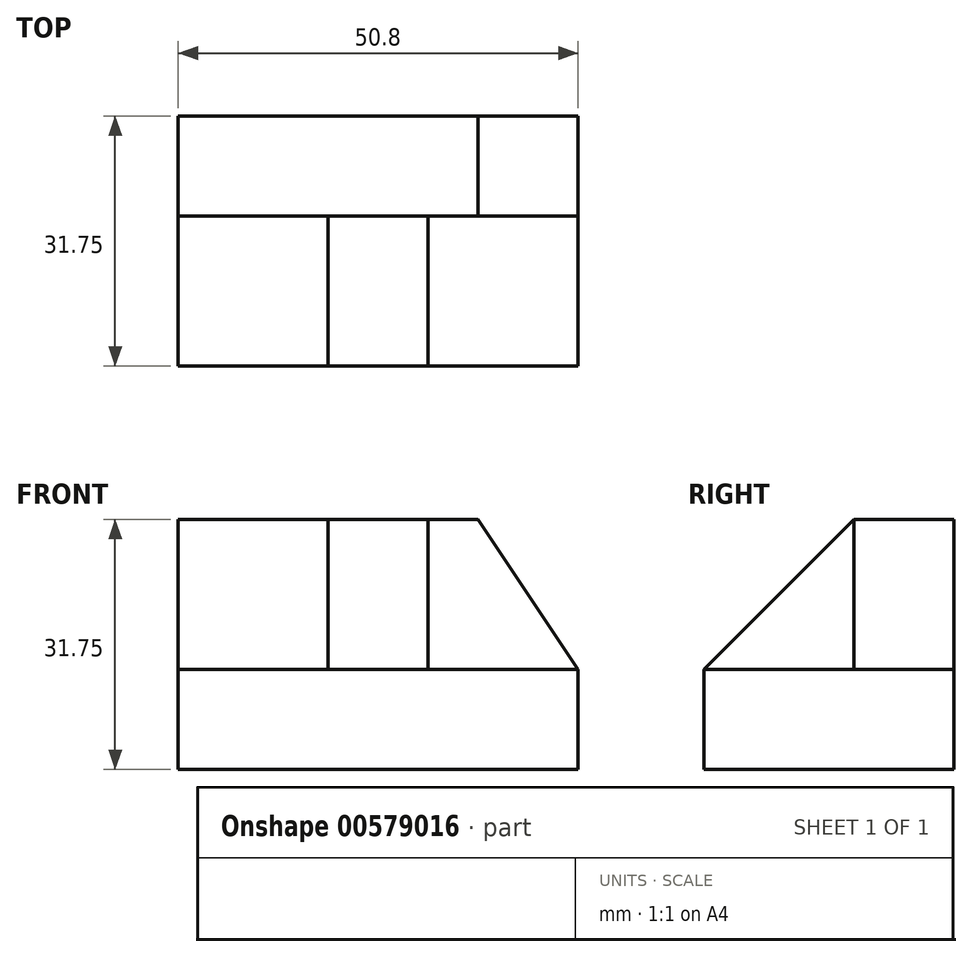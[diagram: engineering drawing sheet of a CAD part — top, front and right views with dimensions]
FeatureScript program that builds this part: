
annotation { "Feature Type Name" : "Feature", "Feature Type Description" : "" }
export const myFeature = defineFeature(function(context is Context, id is Id, definition is map)
    precondition{}
    {
        {
            var Q0;
            Q0=qCreatedBy(makeId("Front.planeOp"),FACE);
            var sketch = newSketch(context, id + "F0", { "sketchPlane" : qUnion([Q0])});
            skLineSegment(sketch, "E0", {"start": v(-68.76, 0) * mm, "end": v(-17.96, 0) * mm});
            skLineSegment(sketch, "E1", {"start": v(-17.96, 0) * mm, "end": v(-17.96, 31.75) * mm});
            skLineSegment(sketch, "E2", {"start": v(-17.96, 31.75) * mm, "end": v(-68.76, 31.75) * mm});
            skLineSegment(sketch, "E3", {"start": v(-68.76, 31.75) * mm, "end": v(-68.76, 0) * mm});
            skSolve(sketch);
        }
        {
            var Q0;
            Q0=makeQuery(id+"F0.imprint","IMPRINT",FACE,{"disambiguationData":[TD([[makeQuery(id+"F0.imprint","IMPRINT",EDGE,{"derivedFrom":sQuery(id+"F0.wireOp",EDGE,"E0")}),1.0]])]});
            extrude(context, id + "F1", {"entities" : qUnion([Q0]), "depth" : 31.75 * mm, "offsetDistance" : 25.4 * mm});
        }
        {
            var Q0;
            Q0=makeQuery(id+"F1.opExtrude","SWEPT_FACE",FACE,{"disambiguationData":[OSD([sQuery(id+"F0.wireOp",EDGE,"E3")])]});
            var sketch = newSketch(context, id + "F2", { "sketchPlane" : qUnion([Q0])});
            skLineSegment(sketch, "E4", {"start": v(31.75, 0) * mm, "end": v(31.75, 12.7) * mm});
            skLineSegment(sketch, "E5", {"start": v(31.75, 12.7) * mm, "end": v(12.7, 12.7) * mm});
            skLineSegment(sketch, "E6", {"start": v(12.7, 12.7) * mm, "end": v(12.7, 31.75) * mm});
            skSolve(sketch);
        }
        {
            var Q0;
            {var subQ0=sQuery(id+"F2.wireOp",EDGE,"E5");Q0=makeQuery(id+"F2.imprint","IMPRINT",FACE,{"disambiguationData":[TD([[makeQuery(id+"F2.imprint","IMPRINT",EDGE,{"derivedFrom":subQ0}),-1.0]])]});}
            extrude(context, id + "F3", {"entities" : qUnion([Q0]), "operationType" : NewBodyOperationType.REMOVE, "oppositeDirection" : true, "depth" : 19.05 * mm, "offsetDistance" : 25.4 * mm});
        }
        {
            var Q0;
            Q0=makeQuery(id+"F3.boolean.opBoolean","COPY",FACE,{"derivedFrom":makeQuery(id+"F3.opExtrude","CAP_FACE",FACE,{"disambiguationData":[OSD([sQuery(id+"F0.wireOp",EDGE,"E2"),sQuery(id+"F0.wireOp",EDGE,"E3"),sQuery(id+"F2.wireOp",EDGE,"E5"),sQuery(id+"F2.wireOp",EDGE,"E6")])],"isStart":false})});
            var sketch = newSketch(context, id + "F4", { "sketchPlane" : qUnion([Q0])});
            skLineSegment(sketch, "E7", {"start": v(12.7, 31.75) * mm, "end": v(31.75, 12.7) * mm});
            skLineSegment(sketch, "E8", {"start": v(31.75, 12.7) * mm, "end": v(31.75, 31.75) * mm});
            skLineSegment(sketch, "E9", {"start": v(31.75, 31.75) * mm, "end": v(12.7, 31.75) * mm});
            skSolve(sketch);
        }
        {
            var Q0;
            Q0=makeQuery(id+"F4.imprint","IMPRINT",FACE,{"disambiguationData":[TD([[makeQuery(id+"F4.imprint","IMPRINT",EDGE,{"derivedFrom":sQuery(id+"F4.wireOp",EDGE,"E7")}),1.0]])]});
            extrude(context, id + "F5", {"entities" : qUnion([Q0]), "operationType" : NewBodyOperationType.REMOVE, "oppositeDirection" : true, "depth" : 12.7 * mm, "offsetDistance" : 25.4 * mm});
        }
        {
            var Q0;
            Q0=makeQuery(id+"F1.opExtrude","SWEPT_FACE",FACE,{"disambiguationData":[OSD([sQuery(id+"F0.wireOp",EDGE,"E1")])]});
            var sketch = newSketch(context, id + "F6", { "sketchPlane" : qUnion([Q0])});
            skLineSegment(sketch, "E10", {"start": v(-31.75, 0) * mm, "end": v(-31.75, 12.7) * mm});
            skLineSegment(sketch, "E11", {"start": v(-31.75, 12.7) * mm, "end": v(-12.7, 12.7) * mm});
            skLineSegment(sketch, "E12", {"start": v(-12.7, 12.7) * mm, "end": v(-12.7, 31.75) * mm});
            skSolve(sketch);
        }
        {
            var Q0;
            {var subQ0=sQuery(id+"F6.wireOp",EDGE,"E11");Q0=makeQuery(id+"F6.imprint","IMPRINT",FACE,{"disambiguationData":[TD([[makeQuery(id+"F6.imprint","IMPRINT",EDGE,{"derivedFrom":subQ0}),1.0]])]});}
            extrude(context, id + "F7", {"entities" : qUnion([Q0]), "operationType" : NewBodyOperationType.REMOVE, "oppositeDirection" : true, "depth" : 19.05 * mm, "offsetDistance" : 25.4 * mm});
        }
        {
            var Q0;
            Q0=makeQuery(id+"F7.boolean.opBoolean","COPY",FACE,{"derivedFrom":makeQuery(id+"F7.opExtrude","SWEPT_FACE",FACE,{"disambiguationData":[OSD([sQuery(id+"F6.wireOp",EDGE,"E12")])]})});
            var sketch = newSketch(context, id + "F8", { "sketchPlane" : qUnion([Q0])});
            skLineSegment(sketch, "E13", {"start": v(-37.01, 31.75) * mm, "end": v(-30.66, 31.75) * mm});
            skLineSegment(sketch, "E14", {"start": v(-30.66, 31.75) * mm, "end": v(-17.96, 12.7) * mm});
            skSolve(sketch);
        }
        {
            var Q0;
            {var subQ0=sQuery(id+"F8.wireOp",EDGE,"E14");Q0=makeQuery(id+"F8.imprint","IMPRINT",FACE,{"disambiguationData":[TD([[makeQuery(id+"F8.imprint","IMPRINT",EDGE,{"derivedFrom":subQ0}),1.0]])]});}
            extrude(context, id + "F9", {"entities" : qUnion([Q0]), "operationType" : NewBodyOperationType.REMOVE, "oppositeDirection" : true, "depth" : 25.4 * mm, "offsetDistance" : 25.4 * mm});
        }
    });
